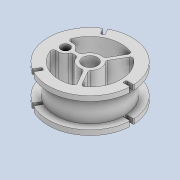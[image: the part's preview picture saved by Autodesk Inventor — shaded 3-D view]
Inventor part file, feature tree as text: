
AUTODESK INVENTOR PART (.ipt)
format: ipt  version: 2020 (Build 240168000, 168)  size: 400,384 bytes
history: native  units: mm
features: extrude x6, sketch x6, fillet x4, projected_geometry x4, pattern_circular x1
ambient origin geometry x8: Origin, YZ Plane, XZ Plane, XY Plane, X Axis, Y Axis, Z Axis, Center Point
bodies: Solid1 (feature_tree)
feature tree (21):
  extrude  "Extrusion1"  Depth=3.0mm
  extrude  "Extrusion2"  Depth=0.7mm
  extrude  "Extrusion3"  Depth=0.7mm
  extrude  "Extrusion4"  Depth=5.0mm
  extrude  "Extrusion5"  Depth=7.0mm TaperAngle=0.0deg
  pattern_circular  "Circular Pattern1"  [2 undecoded]
  fillet  "Fillet1"  Radius=1.5mm
  fillet  "Fillet2"  Radius=1.0mm
  extrude  "Extrusion6"  Depth=0.5mm TaperAngle=0.0deg
  fillet  "Fillet3"  [1 undecoded]
  fillet  "Fillet4"  Radius=3.0mm
  sketch  "Sketch1"  dims[d0=14.0mm d1=3.0mm]
  sketch  "Sketch2"  dims[d2=0.7mm d3=0.7mm]
  projected_geometry  "Projected Loop1"
  sketch  "Sketch3"  dims[d4=3.5mm d5=0.7mm]
  projected_geometry  "Projected Loop2"
  sketch  "Sketch4"  dims[d6=30.0mm d8=360.0deg d10=5.0mm]
  projected_geometry  "Projected Loop3"
  sketch  "Sketch5"  dims[d11=3.0mm d12=7.0mm d13=0.0mm]
  projected_geometry  "Projected Loop4"
  sketch  "Sketch6"  dims[d14=1.8mm d15=19.5mm d16=0.0mm d17=1.5mm d18=1.0mm d19=0.0mm d20=1.0mm d21=0.0mm d22=60.0deg d23=3.0mm d24=0.7mm d25=20.0mm d26=0.0mm d27=30.0mm d28=360.0deg d30=0.2mm d31=0.5mm d32=5.5mm d33=3.0mm d34=0.0mm d35=0.5mm d36=0.5mm]
note: 3 required parameter values undecoded (feature->parameter linkage not recoverable at this tier; creation-order binding heuristic only, values carry confidence <= 0.55)
